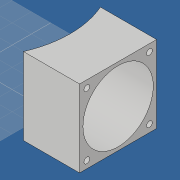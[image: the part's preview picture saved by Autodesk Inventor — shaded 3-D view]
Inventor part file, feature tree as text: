
AUTODESK INVENTOR PART (.ipt)
format: ipt  version: 2019 (Build 230136000, 136)  size: 118,272 bytes
history: native  units: mm
features: extrude x2, sketch x2, other x1
ambient origin geometry x8: Origin, YZ Plane, XZ Plane, XY Plane, X Axis, Y Axis, Z Axis, Center Point
bodies: Volumenkörper1 (feature_tree)
feature tree (5):
  other  "<userpath>\OneDrive\Dokumente\Inventor\Absauganlage\Absauganlage_Params.xlsx"
  extrude  "Extrusion1"  Depth=4.9mm
  extrude  "Extrusion2"  Depth=150.0mm
  sketch  "Skizze1"  dims[d0=200.0mm d1=4.9mm]
  sketch  "Skizze2"  dims[d2=150.0mm d3=80.0mm d4=80.0mm d5=0.0mm d6=73.0mm d7=75.0mm d8=0.0mm d9=65.0mm d10=6.0mm]
